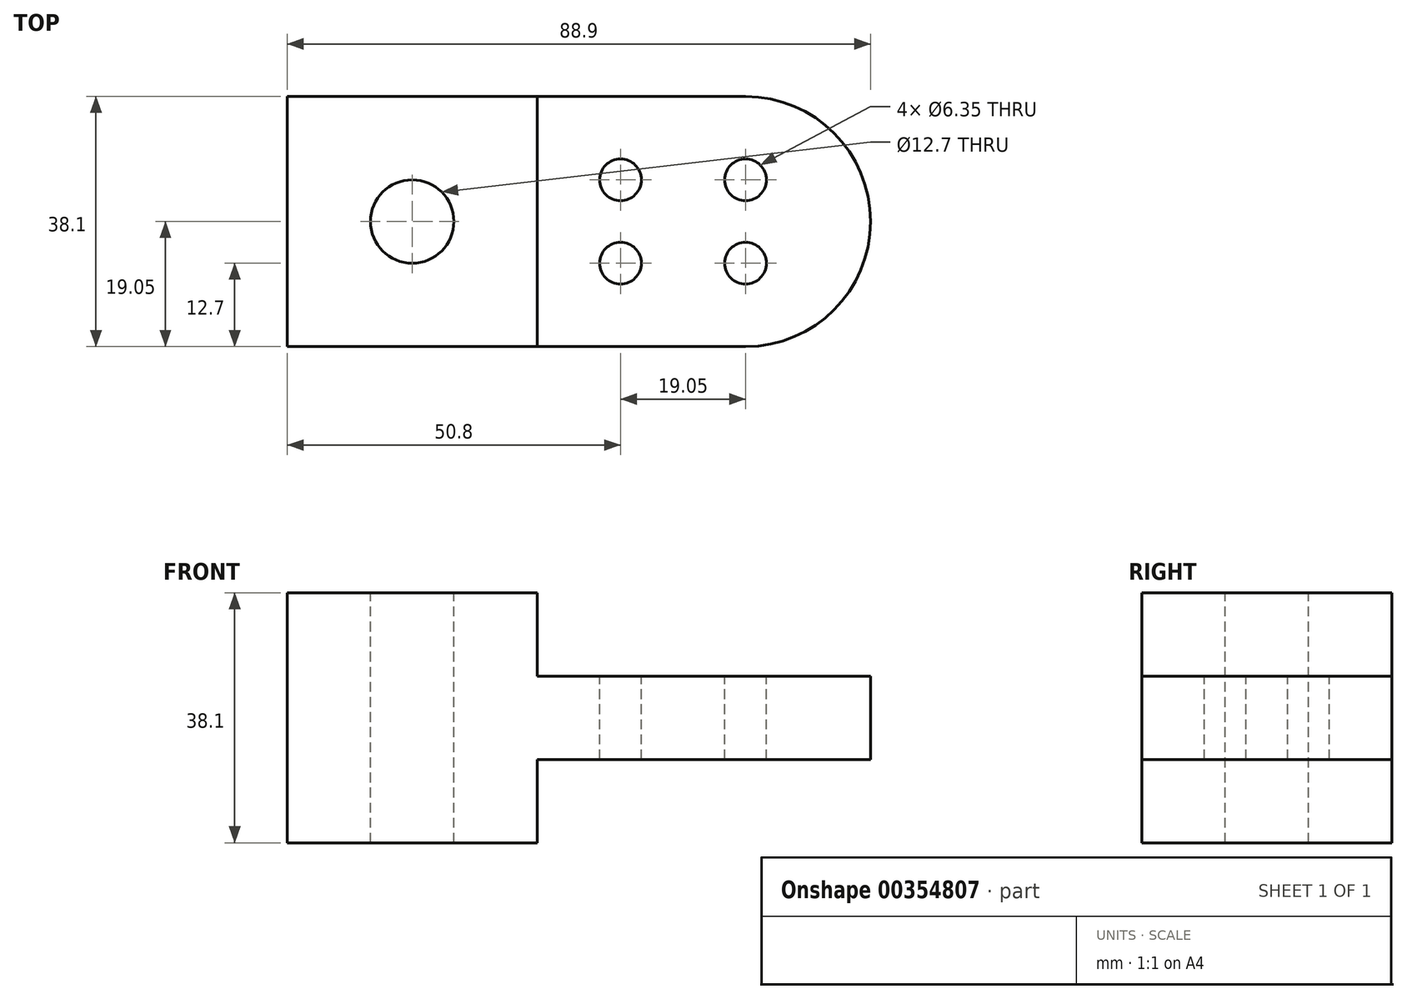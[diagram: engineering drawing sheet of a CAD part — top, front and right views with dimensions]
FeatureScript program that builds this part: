
annotation { "Feature Type Name" : "Feature", "Feature Type Description" : "" }
export const myFeature = defineFeature(function(context is Context, id is Id, definition is map)
    precondition{}
    {
        {
            var Q0;
            Q0=qCreatedBy(makeId("Top.planeOp"),FACE);
            var sketch = newSketch(context, id + "F0", { "sketchPlane" : qUnion([Q0])});
            skLineSegment(sketch, "E0.bottom", {"start": v(0, 0) * mm, "end": v(38.1, 0) * mm});
            skLineSegment(sketch, "E0.top", {"start": v(0, 38.1) * mm, "end": v(38.1, 38.1) * mm});
            skLineSegment(sketch, "E0.left", {"start": v(0, 0) * mm, "end": v(0, 38.1) * mm});
            skLineSegment(sketch, "E0.right", {"start": v(38.1, 0) * mm, "end": v(38.1, 38.1) * mm});
            skLineSegment(sketch, "E1", {"start": v(38.1, 38.1) * mm, "end": v(69.85, 38.1) * mm});
            skLineSegment(sketch, "E2", {"start": v(69.85, 38.1) * mm, "end": v(69.85, 0) * mm, "construction": true});
            skLineSegment(sketch, "E3", {"start": v(69.85, 0) * mm, "end": v(38.1, 0) * mm});
            skArc(sketch, "E4", {"start": v(69.85, 0) * mm, "mid": v(88.9, 19.05) * mm, "end": v(69.85, 38.1) * mm});
            skSolve(sketch);
        }
        {
            var Q0;
            Q0=makeQuery(id+"F0.imprint","IMPRINT",FACE,{"disambiguationData":[TD([[makeQuery(id+"F0.imprint","IMPRINT",EDGE,{"derivedFrom":sQuery(id+"F0.wireOp",EDGE,"E0.bottom")}),1.0]])]});
            extrude(context, id + "F1", {"entities" : qUnion([Q0]), "depth" : 38.1 * mm});
        }
        {
            var Q0;
            Q0=makeQuery(id+"F0.imprint","IMPRINT",FACE,{"disambiguationData":[TD([[makeQuery(id+"F0.imprint","IMPRINT",EDGE,{"derivedFrom":sQuery(id+"F0.wireOp",EDGE,"E0.right")}),-1.0]])]});
            extrude(context, id + "F2", {"entities" : qUnion([Q0]), "operationType" : NewBodyOperationType.ADD, "depth" : 25.4 * mm});
        }
        {
            var Q0;
            Q0=makeQuery(id+"F0.imprint","IMPRINT",FACE,{"disambiguationData":[TD([[makeQuery(id+"F0.imprint","IMPRINT",EDGE,{"derivedFrom":sQuery(id+"F0.wireOp",EDGE,"E0.right")}),-1.0]])]});
            extrude(context, id + "F3", {"entities" : qUnion([Q0]), "operationType" : NewBodyOperationType.REMOVE, "depth" : 12.7 * mm});
        }
        {
            var Q0;
            Q0=makeQuery(id+"F1.opExtrude","CAP_FACE",FACE,{"disambiguationData":[OSD([sQuery(id+"F0.wireOp",EDGE,"E0.bottom"),sQuery(id+"F0.wireOp",EDGE,"E0.top"),sQuery(id+"F0.wireOp",EDGE,"E0.left"),sQuery(id+"F0.wireOp",EDGE,"E0.right")])],"isStart":false});
            var sketch = newSketch(context, id + "F4", { "sketchPlane" : qUnion([Q0])});
            skCircle(sketch, "E5", {"center": v(19.05, 19.05) * mm, "radius": 6.35 * mm});
            skPoint(sketch, "E5.centerSnap0", {"position": v(0, 19.05) * mm});
            skPoint(sketch, "E5.centerSnap1", {"position": v(19.05, 38.1) * mm});
            skSolve(sketch);
        }
        {
            var Q0;
            Q0=makeQuery(id+"F2.opExtrude","CAP_FACE",FACE,{"disambiguationData":[OSD([sQuery(id+"F0.wireOp",EDGE,"E0.right"),sQuery(id+"F0.wireOp",EDGE,"E1"),sQuery(id+"F0.wireOp",EDGE,"E3"),sQuery(id+"F0.wireOp",EDGE,"E4")])],"isStart":false});
            var sketch = newSketch(context, id + "F5", { "sketchPlane" : qUnion([Q0])});
            skCircle(sketch, "E6", {"center": v(50.8, 25.4) * mm, "radius": 3.18 * mm});
            skCircle(sketch, "E7", {"center": v(50.8, 12.7) * mm, "radius": 3.18 * mm});
            skCircle(sketch, "E8", {"center": v(69.85, 25.4) * mm, "radius": 3.18 * mm});
            skCircle(sketch, "E9", {"center": v(69.85, 12.7) * mm, "radius": 3.18 * mm});
            skSolve(sketch);
        }
        {
            var Q0;
            Q0 = qSketchRegion(id + "F5", true);
            var Q1;
            Q1=makeQuery(id+"F4.imprint","IMPRINT",FACE,{"disambiguationData":[TD([[makeQuery(id+"F4.imprint","IMPRINT",EDGE,{"derivedFrom":sQuery(id+"F4.wireOp",EDGE,"E5")}),1.0]])]});
            extrude(context, id + "F6", {"entities" : qUnion([Q0, Q1]), "operationType" : NewBodyOperationType.REMOVE, "endBound" : BoundingType.THROUGH_ALL, "oppositeDirection" : true, "depth" : 25.4 * mm});
        }
    });
